# Revit family: VL2E-GP150xWSxxxB
name_source: partatom
category: Leuchten
units: mm (PartAtom-declared; Revit-internal decimal feet)

## family parameters
Basisbauteil = Fläche
Beim Laden mit Abzugskörper schneiden = Nein
Bemaßung runder Anschluss = Durchmesser verwenden
Beschriftungsausrichtung beibehalten = Nein
Gemeinsam genutzt = Nein
Lichtquelle = Ja
OmniClass-Nummer = 23.80.70.11
OmniClass-Titel = Luminaries for Internal Lighting
Raumberechnungspunkt = Nein
Teiletyp = Normal

## types (10) — shared parameters
Baugruppenkennzeichen = D5020200
Datei für fotometrisches Netz = Master_VL1GP1486-5RFWS840B0900.IES
Emissionsform beim Rendern sichtbar = Nein
Farbfilter = 16777215
Farbtemperaturverschiebung bei Dämpfen der Lampe = <Keine Auswahl>
Hersteller = RIDI Leuchten GmbH
Lampe = LED
Neigungswinkel = 90.00°
URL = www.ridi.de
Von Breite des Rechtecks ausssenden = 1479 mm  [stored 4.85236 ft]
Von Länge des Rechtecks aussenden = 61 mm  [stored 0.200131 ft]
brand = RIDI
conformity mark = CE
electrical safety class = 1
height = 64 mm  [stored 0.209974 ft]
ingress protection (IP) code = IP20
length = 1500 mm  [stored 4.92126 ft]
nominal frequency = 50-60Hz
nominal voltage = 230
voltage type (AC, DC, UC) = AC
width = 67 mm
zero-valued in all types: Vorgabe-Ansicht

## per-type parameters (varying)
| type | Modell | Scheinlast | rated input power | weight |
| VL2E-GP150-5FLWS840B1000 | 2550015 | 63 VA | 63 | 1.7 kg |
| VL2E-GP150-7DAWS840B1000 | 2560015 | 65 VA | 65 | 1.7 kg |
| VL2E-GP150-13DAWS840B1000-ED | 2560015//381 | 65 VA | 65 | 2.9 kg |
| VL2E-GP150-13DAWS840B1000-UR | 2560015//366 | 65 VA | 65 | 1.9 kg |
| VL2E-GP150-13DAWS840B1000-Z | 2560015//367 | 65 VA | 65 | 1.7 kg |
| VL2E-GP150-7DAWS840B0600 | 2550196 | 35 VA | 35 | 1.7 kg |
| VL2E-GP150-7DAWS840B0800 | 2550208 | 49 VA | 49 | 1.7 kg |
| VL2E-GP150-7FLWS840B1000-ED | 2550015//377 | 63 VA | 63 | 2.9 kg |
| VL2E-GP150-7FLWS840B1000-UR | 2550015//373 | 63 VA | 63 | 1.9 kg |
| VL2E-GP150-7FLWS840B1000-Z | 2550015//329 | 63 VA | 63 | 1.7 kg |

note: column(s) folded — value = type name in every type: product name

note: [stored X ft] marks values corroborated as IEEE doubles in the binary element streams (Revit-internal decimal feet)
